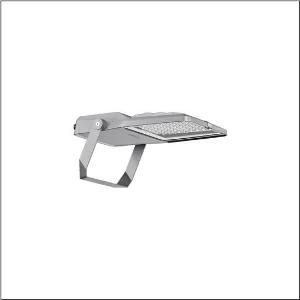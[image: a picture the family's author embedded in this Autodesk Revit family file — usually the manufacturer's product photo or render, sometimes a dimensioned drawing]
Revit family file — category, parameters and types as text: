
# Revit family: floodlight_fl_21_iq_mini___pl61_5xa7772c2c1a_b30e
name_source: partatom
category: Lighting Fixtures
units: mm (PartAtom-declared; Revit-internal decimal feet)

## family parameters
Cut with Voids When Loaded = No
Host = Face
Light Source = No
Part Type = Normal
Room Calculation Point = No
Round Connector Dimension = Use Diameter
Shared = No

## types (1)
- --- (1 x LED, 11980 lm, 87.2 W, 3000K)
    Apparent Load = 87 VA
    CIE Flux Codes = 33 65 98 100 100
    Color Rendering = 70
    Color Temperature = 3000K
    Default Elevation = 1800 mm
    Description = Floodlight FL 21 iQ mini, floodlight, primary light control with lens, of PMMA, primary optical cover: protective disc, of toughened safety glass, transparent, light distribution: PL61, light emission: direct distribution, installation type: surface-mounted, LED, High Power LED, rated luminous flux: 11.980lm, luminous efficacy: 137lm/W, light colour: 730, colour temperature: 3000K, control: Street-Remote, Auto-Match, Temp-Guard, Night-Set, Smart-Wire, Desk-Remote (wireless, voltage-free reading and setting of iQ features in the workshop via application-optimized NFC function/RFID function), optimised constant luminous flux control (CLO 2.0), with terminal, 6-pole, mains connection: 220..240V, AC, 50/60Hz, start of lifetime: 87W, end of service life: 92W, reduction: 40W, luminaire housing, of diecast aluminium, powder-coated, Siteco® metallic grey (DB 702S), corrosivity category C5 mid according to DIN EN ISO 12944, sealing non-destructively replaceable, mounting bracket, of steel, galvanised, powder-coated, Siteco® metallic grey (DB 702S), protection rating (complete): IP66, insulation class (complete): insulation class II (safety insulation), certification: CE, ENEC, VDE, protection symbol: D, impact resistance: IK08, permissible operating ambient temperature: -40..+40°C, permissible operating ambient temperature for outdoor applications: -40..+50°C, standard: DIN EN 12944, LABS conformity tested according to VDMA 24364:2018-05, packaging unit: 1 piece

Light Distribution: PL61
    Height = 70 mm
    Lamp = 1 x LED
    Lamp Light Flux = 11980 lm
    Lamp Power = 87.2 W
    Lamp count = 1
    Length = 485 mm
    Luminous efficacy = 137 lm/W
    Manufacturer = Siteco
    ModVariant = No
    Model = 5XA7772C2C1A
    Number of Poles = 1
    OnlyDefault = Yes
    Power Factor = 1
    Product Name = Floodlight FL 21 iQ mini | PL61
    Product group = floodlight | pylon annexe
    ProductGroupID = 6200
    Protection Class = Protection class II
    Protection Degree = IP 66
    RLX_Detail_Level = 1
    RLX_Emergency_Light_Flux = 0 lm
    RLX_Emergency_Type = 0
    RLX_Emergency_Type_DB = No
    RlxData = <blob elided: 96473 chars, md5=c43f1e48>
    Socket = socket
    Standby Power = 0 W
    System Light Flux = 11980 lm
    System Power = 87 W
    Type Comments = factory setting: luminous flux: 100 % | dim-lin: 254 | 456 mA
    Type Image = l_1006845.jpg
    URL = http://relux.com
    VarID = @adj_124043
    Voltage = 0 V
    Weight = 0.00 kg
    Width = 337 mm

## geometry (parser evidence)
native form markers: Blend x4, Sweep x14
no freeform markers — native parametric forms only
